# Revit family: 208_6844ec6d8aa84b5f8be4da512e3c3c
name_source: partatom
category: Air Terminals
revit_build: Autodesk Revit 2018 (Build: 20170223_1515(x64)
units: mm (PartAtom-declared; Revit-internal decimal feet)

## family parameters
Always vertical = Yes
Cut with Voids When Loaded = No
Part Type = Normal
Room Calculation Point = Yes
Round Connector Dimension = Use Diameter
Shared = No
Work Plane-Based = No

## types (1)
- 02158
    CLBTZ = 0 mm  [stored 0 ft]
    CL_Location_5000 = 5000 mm  [stored 16.4042 ft]
    D = 51 mm
    DL = 10 mm  [stored 0.0328084 ft]
    DL__ve = -10 mm  [stored -0.0328084 ft]
    Description = Vacuum Cleaner Exhaust outlet
    H2 = 58 mm  [stored 0.190289 ft]
    H_ARR = 0 mm  [stored 0 ft]
    L_ARR = 400 mm  [stored 1.31234 ft]
    MC Product Code = 02158
    Manufacturer = Flexit
    QmdConnectorList = 201;D
    R = 26 mm
    R0 = 2 mm  [stored 0.00656168 ft]
    URL = www.flexit.no
    W2 = 45 mm  [stored 0.147638 ft]
    W_ARR = 400 mm  [stored 1.31234 ft]
    magiPartTypeId = 208
    magiProductFamilyId = 6844ec6d8aa84b5f8be4da512e3c3c
    magiProductId = aa335138981046aab68fd7ec20c927

note: [stored X ft] marks values corroborated as IEEE doubles in the binary element streams (Revit-internal decimal feet)

## geometry (parser evidence)
native form markers: Sweep x2
no freeform markers — native parametric forms only
